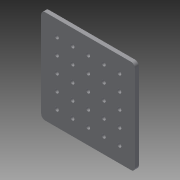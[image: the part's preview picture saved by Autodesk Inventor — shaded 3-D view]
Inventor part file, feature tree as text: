
AUTODESK INVENTOR PART (.ipt)
format: ipt  version: 2015 (Build 190159000, 159)  size: 124,416 bytes
history: native  units: mm
features: extrude x1, fillet x1, sketch x1
ambient origin geometry x8: Origin, YZ Plane, XZ Plane, XY Plane, X Axis, Y Axis, Z Axis, Center Point
bodies: Solid1 (feature_tree)
feature tree (3):
  extrude  "Extrusion1"  Depth=120.0mm
  fillet  "Fillet1"  Radius=5.0mm
  sketch  "Sketch1"  dims[d0=120.0mm d1=120.0mm d2=5.0mm d4=20.0mm d5=20.0mm d6=50.0mm d8=20.0mm d9=50.0mm d11=20.0mm d14=5.0mm d15=0.0mm d16=5.0mm]
